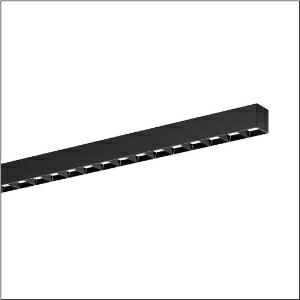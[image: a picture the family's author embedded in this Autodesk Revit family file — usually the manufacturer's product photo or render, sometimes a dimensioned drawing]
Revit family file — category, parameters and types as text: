
# Revit family: silica_r__21_51mx24dc3abb_157e
name_source: partatom
category: Lighting Fixtures
units: mm (PartAtom-declared; Revit-internal decimal feet)

## family parameters
Cut with Voids When Loaded = No
Host = Face
Light Source = No
Part Type = Normal
Room Calculation Point = No
Round Connector Dimension = Use Diameter
Shared = No

## types (1)
- --- (1 x LED, 10800 lm, 79 W, 3000K)
    Apparent Load = 79 VA
    CIE Flux Codes = 74 94 99 100 100
    Color Rendering = 80
    Color Temperature = 3000K
    Default Elevation = 1800 mm
    Description = Silica® 21, office luminaire, primary light control with darklight reflector, of PMMA, black, CAT 2 (L<= 3000cd/m²), light emission: direct distribution, primary light characteristic: asymmetric, installation type: surface-mounted, LED, rated luminous flux: 10.800lm, luminous efficacy: 137lm/W, light colour: 830, colour temperature: 3000K, with terminal, 3+2-pole, max. 2.5mm², mains connection: 220..240V, AC, 50/60Hz, rated input power: 79W, luminaire housing, of aluminium, jet black (RAL 9005), length: 3.004mm, width: 53mm, height: 53mm, protection rating (complete): IP20, insulation class (complete): insulation class I (protective earthing), certification: CE, permissible operating ambient temperature: 0..+35°C, standard: EN 50419, packaging unit: 1 piece
    Height = 0 mm  [stored 0 ft]
    Lamp = 1 x LED
    Lamp Light Flux = 10800 lm
    Lamp Power = 79 W
    Lamp count = 1
    Length = 3004 mm
    Luminous efficacy = 137 lm/W
    Manufacturer = Siteco
    ModVariant = No
    Model = 51MX24DC3ABB
    Mounting Place = Ceiling
    Mounting Type = Recessed
    Number of Poles = 1
    OnlyDefault = Yes
    Power Factor = 1
    Product Name = Silica® 21
    Product group = office luminaire | ceiling recessed
    ProductGroupID = 401
    Protection Class = Protection class I
    Protection Degree = IP 20
    RLX_Detail_Level = 1
    RLX_Emergency_Light_Flux = 0 lm
    RLX_Emergency_Type = 0
    RLX_Emergency_Type_DB = No
    RlxData = <blob elided: 64857 chars, md5=33396d4f>
    Socket = socket
    Standby Power = 0 W
    System Light Flux = 10800 lm
    System Power = 79 W
    Type Comments = factory setting: luminous flux: 100 % | dim-lin: 254 | 448 mA
    Type Image = l_1313577.jpg
    URL = http://relux.com
    VarID = @adj_071677
    Voltage = 0 V
    Weight = 0.00 kg
    Width = 53 mm

note: [stored X ft] marks values corroborated as IEEE doubles in the binary element streams (Revit-internal decimal feet)

## geometry (parser evidence)
native form markers: Blend x4, Sweep x12
no freeform markers — native parametric forms only
